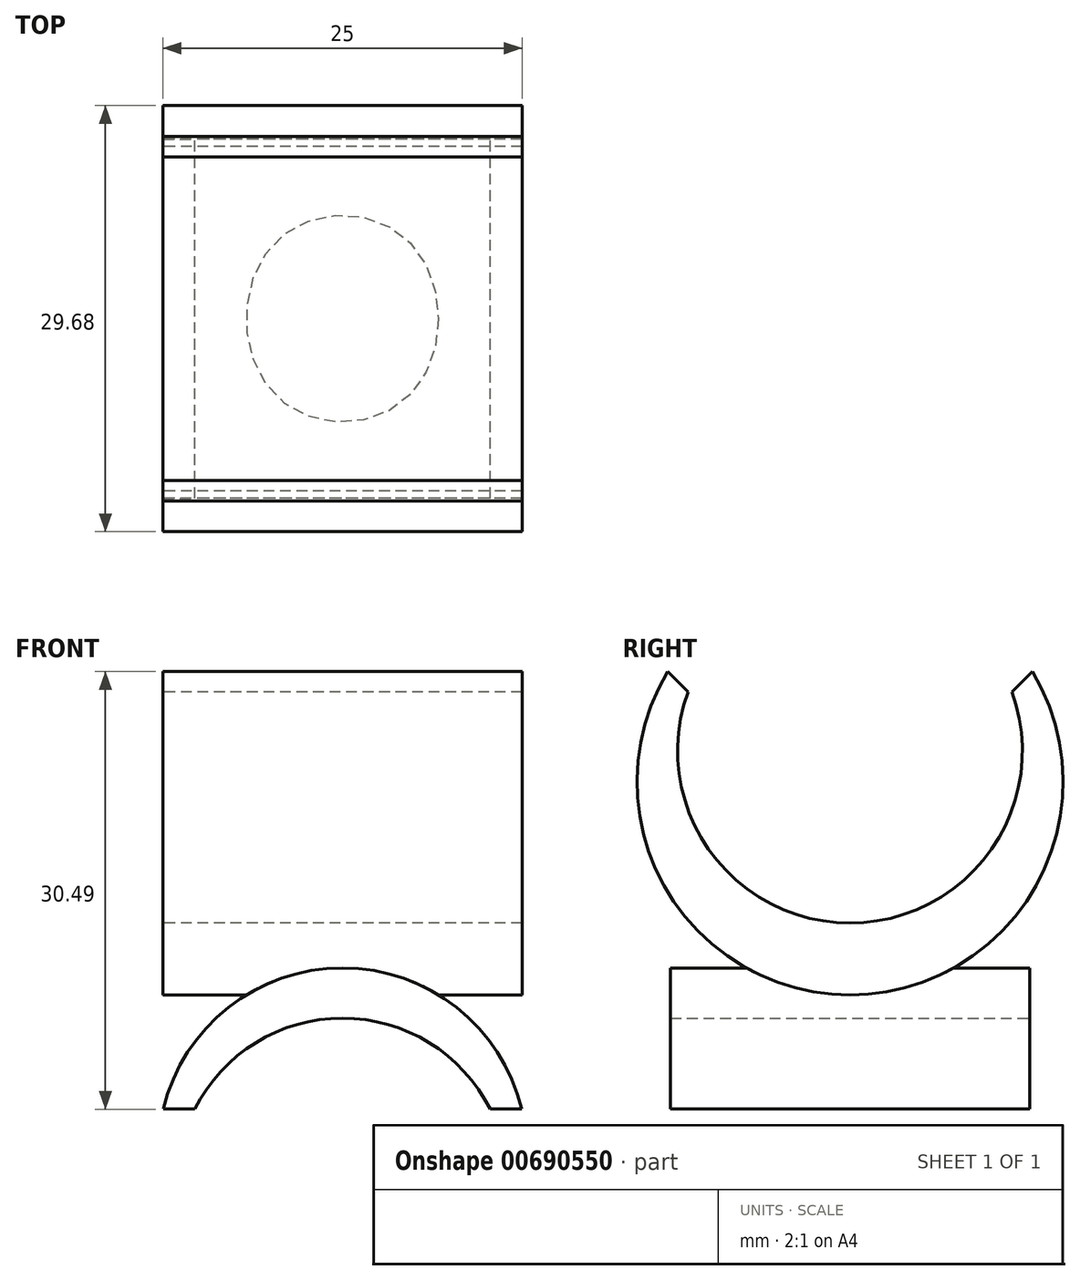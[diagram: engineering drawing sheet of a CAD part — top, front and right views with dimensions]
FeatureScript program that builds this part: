
annotation { "Feature Type Name" : "Feature", "Feature Type Description" : "" }
export const myFeature = defineFeature(function(context is Context, id is Id, definition is map)
    precondition{}
    {
        {
            var Q0;
            Q0=qCreatedBy(makeId("Right.planeOp"),FACE);
            var sketch = newSketch(context, id + "F0", { "sketchPlane" : qUnion([Q0])});
            skCircle(sketch, "E0", {"center": v(0, 0) * mm, "radius": 12 * mm});
            skLineSegment(sketch, "E1", {"start": v(-11.27, 4.1) * mm, "end": v(11.27, 4.1) * mm, "construction": true});
            skLineSegment(sketch, "E2", {"start": v(0, -12) * mm, "end": v(0, -17) * mm});
            skLineSegment(sketch, "E3", {"start": v(-12.7, 5.52) * mm, "end": v(12.7, 5.52) * mm, "construction": true});
            skLineSegment(sketch, "E4", {"start": v(-11.27, 4.1) * mm, "end": v(-12.7, 5.52) * mm});
            skLineSegment(sketch, "E5", {"start": v(11.27, 4.1) * mm, "end": v(12.7, 5.52) * mm});
            skArc(sketch, "E6", {"start": v(-12.7, 5.52) * mm, "mid": v(0, -17) * mm, "end": v(12.7, 5.52) * mm});
            skSolve(sketch);
        }
        {
            var Q0;
            {var subQ0=sQuery(id+"F0.wireOp",EDGE,"E2");Q0=makeQuery(id+"F0.imprint","IMPRINT",FACE,{"disambiguationData":[TD([[makeQuery(id+"F0.imprint","IMPRINT",EDGE,{"derivedFrom":subQ0}),-1.0]])]});}
            var Q1;
            {var subQ0=sQuery(id+"F0.wireOp",EDGE,"E2");Q1=makeQuery(id+"F0.imprint","IMPRINT",FACE,{"disambiguationData":[TD([[makeQuery(id+"F0.imprint","IMPRINT",EDGE,{"derivedFrom":subQ0}),1.0]])]});}
            extrude(context, id + "F1", {"entities" : qUnion([Q0, Q1]), "endBound" : BoundingType.SYMMETRIC, "depth" : 25 * mm, "offsetDistance" : 25 * mm});
        }
        {
            var Q0;
            Q0=qCreatedBy(makeId("Front.planeOp"),FACE);
            var sketch = newSketch(context, id + "F2", { "sketchPlane" : qUnion([Q0])});
            skCircle(sketch, "E7", {"center": v(0, -30.13) * mm, "radius": 11.5 * mm});
            skLineSegment(sketch, "E8", {"start": v(0, -18.63) * mm, "end": v(0, -15.13) * mm});
            skArc(sketch, "E9", {"start": v(12.48, -24.97) * mm, "mid": v(0, -15.13) * mm, "end": v(-12.48, -24.97) * mm});
            skLineSegment(sketch, "E10", {"start": v(12.48, -24.97) * mm, "end": v(10.28, -24.97) * mm});
            skLineSegment(sketch, "E11", {"start": v(-12.48, -24.97) * mm, "end": v(-10.28, -24.97) * mm});
            skSolve(sketch);
        }
        {
            var Q0;
            {var subQ0=sQuery(id+"F2.wireOp",EDGE,"E8");Q0=makeQuery(id+"F2.imprint","IMPRINT",FACE,{"disambiguationData":[TD([[makeQuery(id+"F2.imprint","IMPRINT",EDGE,{"derivedFrom":subQ0}),-1.0]])]});}
            var Q1;
            {var subQ0=sQuery(id+"F2.wireOp",EDGE,"E8");Q1=makeQuery(id+"F2.imprint","IMPRINT",FACE,{"disambiguationData":[TD([[makeQuery(id+"F2.imprint","IMPRINT",EDGE,{"derivedFrom":subQ0}),1.0]])]});}
            extrude(context, id + "F3", {"entities" : qUnion([Q0, Q1]), "operationType" : NewBodyOperationType.ADD, "endBound" : BoundingType.SYMMETRIC, "depth" : 25 * mm, "offsetDistance" : 25 * mm});
        }
    });
